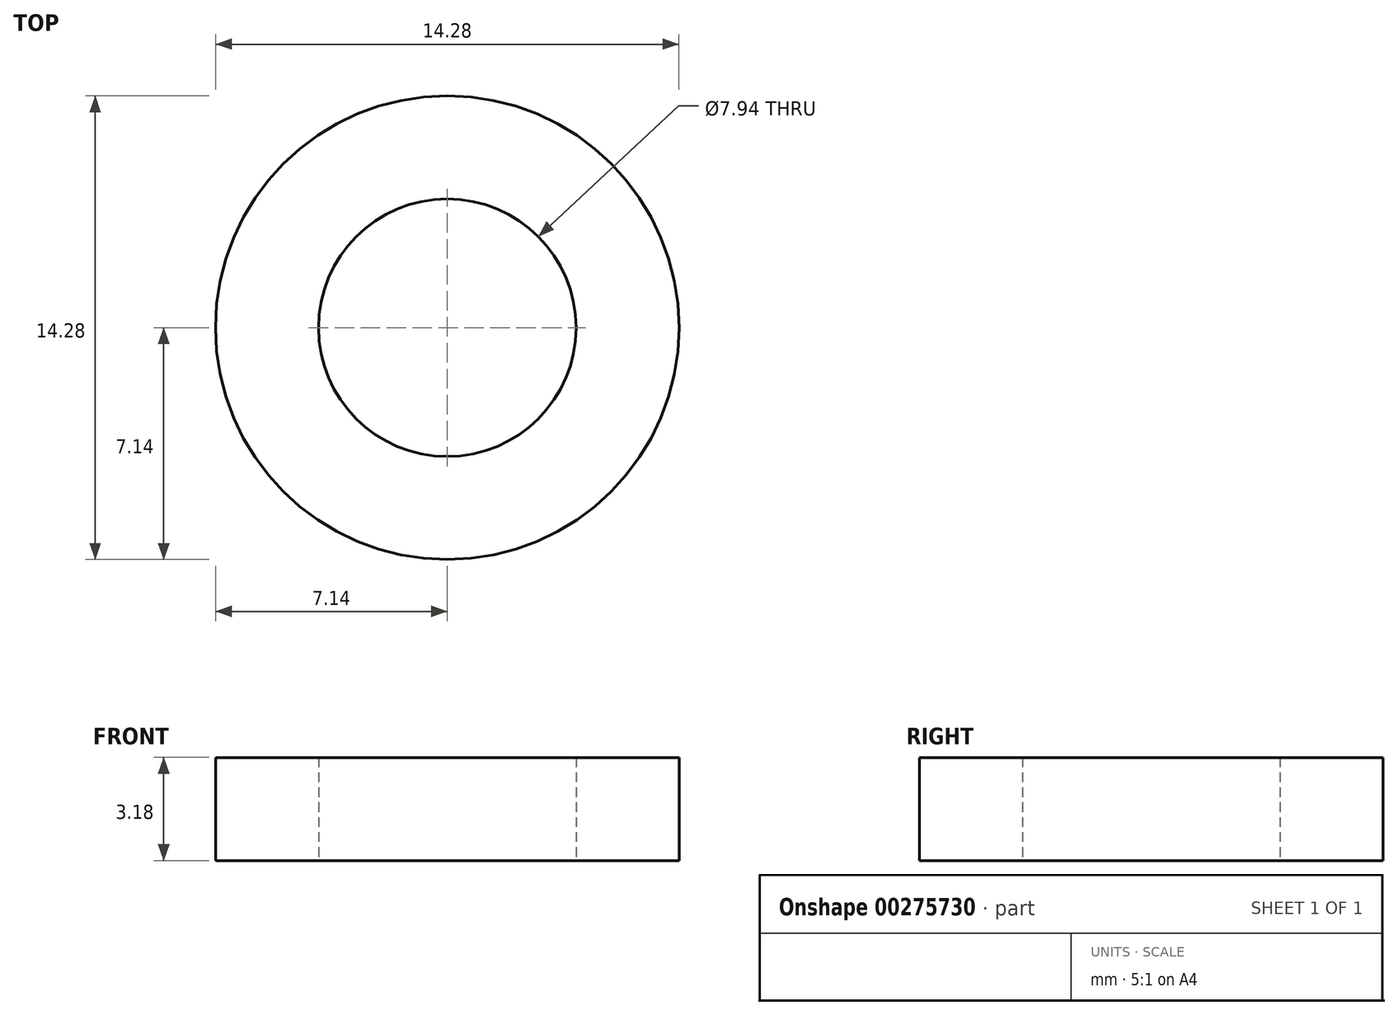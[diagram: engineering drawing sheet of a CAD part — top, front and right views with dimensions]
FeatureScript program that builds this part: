
annotation { "Feature Type Name" : "Feature", "Feature Type Description" : "" }
export const myFeature = defineFeature(function(context is Context, id is Id, definition is map)
    precondition{}
    {
        {
            var Q0;
            Q0=qCreatedBy(makeId("Top.planeOp"),FACE);
            var sketch = newSketch(context, id + "F0", { "sketchPlane" : qUnion([Q0])});
            skCircle(sketch, "E0", {"center": v(0, 0) * mm, "radius": 7.14 * mm});
            skCircle(sketch, "E1", {"center": v(0, 0) * mm, "radius": 3.97 * mm});
            skSolve(sketch);
        }
        {
            var Q0;
            Q0=qSketchRegion(id+"F0",true);
            extrude(context, id + "F1", {"entities" : qUnion([Q0]), "depth" : 3.17 * mm});
        }
    });
